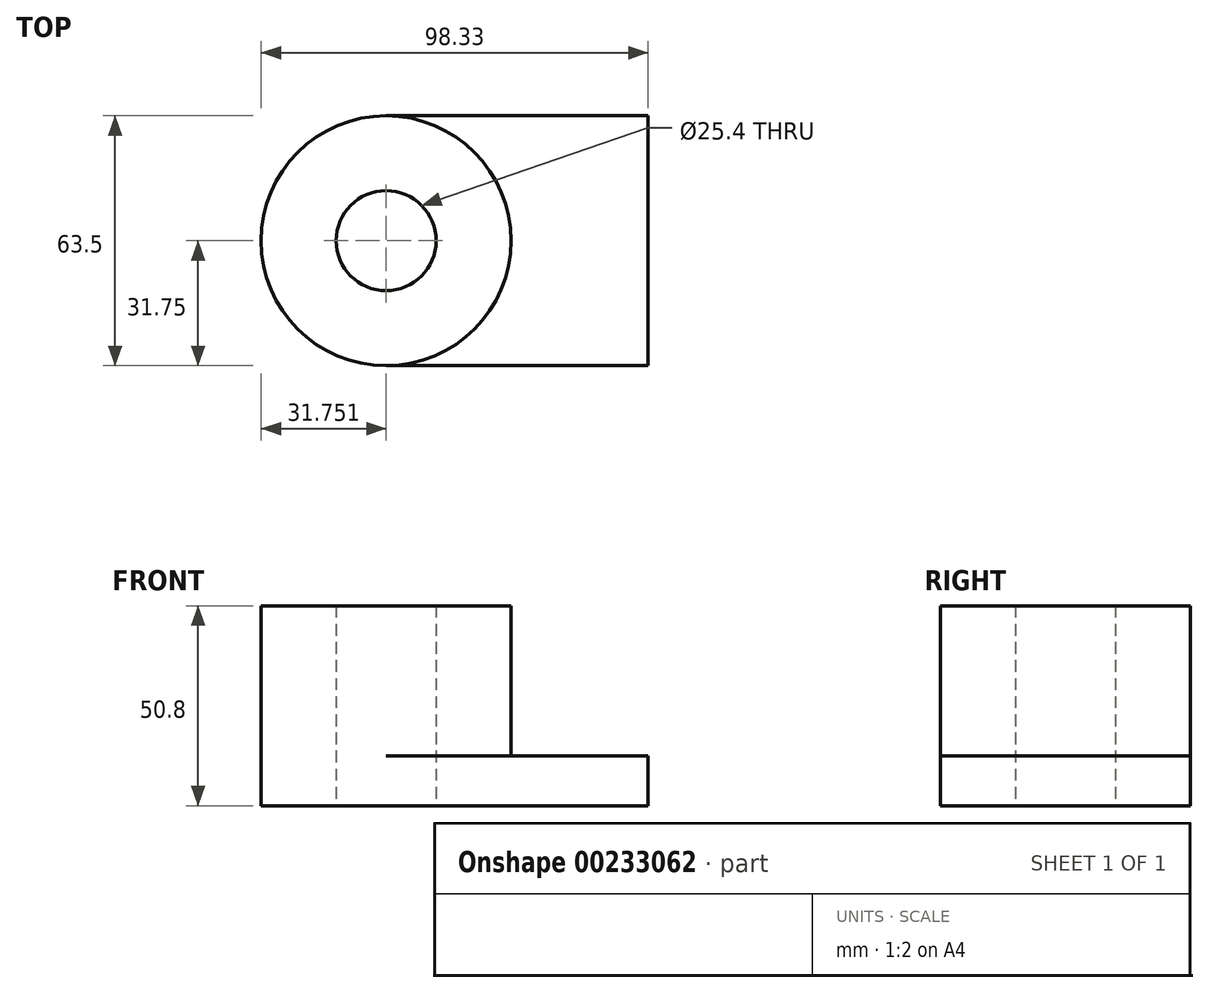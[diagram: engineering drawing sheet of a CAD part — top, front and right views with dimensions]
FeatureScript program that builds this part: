
annotation { "Feature Type Name" : "Feature", "Feature Type Description" : "" }
export const myFeature = defineFeature(function(context is Context, id is Id, definition is map)
    precondition{}
    {
        {
            var Q0;
            Q0=qCreatedBy(makeId("Top.planeOp"),FACE);
            var sketch = newSketch(context, id + "F0", { "sketchPlane" : qUnion([Q0])});
            skLineSegment(sketch, "E0.bottom", {"start": v(-33.29, -31.75) * mm, "end": v(33.29, -31.75) * mm});
            skLineSegment(sketch, "E0.top", {"start": v(-33.29, 31.75) * mm, "end": v(33.29, 31.75) * mm});
            skLineSegment(sketch, "E0.left", {"start": v(-33.29, -31.75) * mm, "end": v(-33.29, 31.75) * mm});
            skLineSegment(sketch, "E0.right", {"start": v(33.29, -31.75) * mm, "end": v(33.29, 31.75) * mm});
            skPoint(sketch, "E0.middle", {"position": v(0, 0) * mm});
            skCircle(sketch, "E1", {"center": v(-33.29, 0) * mm, "radius": 31.75 * mm});
            skCircle(sketch, "E2", {"center": v(-33.29, 0) * mm, "radius": 12.7 * mm});
            skSolve(sketch);
        }
        {
            var Q0;
            Q0 = qSketchRegion(id + "F0", true);
            extrude(context, id + "F1", {"entities" : qUnion([Q0]), "depth" : 12.7 * mm});
        }
        {
            var Q0;
            {var subQ1=sQuery(id+"F0.wireOp",EDGE,"E0.left");var subQ3=sQuery(id+"F0.wireOp",EDGE,"E2");var subQ4=makeQuery(id+"F0.imprint","INTERSECT",VERTEX,{"disambiguationData":[OD(0.0)],"derivedFrom":[subQ1,subQ3]});Q0=makeQuery(id+"F0.imprint","IMPRINT",FACE,{"disambiguationData":[TD([[makeQuery(id+"F0.imprint","IMPRINT",EDGE,{"disambiguationData":[TD([[subQ4,1.0]])],"derivedFrom":subQ3}),-1.0]])]});}
            var Q1;
            {var subQ1=sQuery(id+"F0.wireOp",EDGE,"E0.left");var subQ3=sQuery(id+"F0.wireOp",EDGE,"E2");var subQ4=makeQuery(id+"F0.imprint","INTERSECT",VERTEX,{"disambiguationData":[OD(0.0)],"derivedFrom":[subQ1,subQ3]});Q1=makeQuery(id+"F0.imprint","IMPRINT",FACE,{"disambiguationData":[TD([[makeQuery(id+"F0.imprint","IMPRINT",EDGE,{"disambiguationData":[TD([[subQ4,-1.0]])],"derivedFrom":subQ3}),-1.0]])]});}
            extrude(context, id + "F2", {"entities" : qUnion([Q0, Q1]), "operationType" : NewBodyOperationType.ADD, "depth" : 50.8 * mm});
        }
    });
